# Revit family: Ladder_Caged-Access_ALACO_560-CP
name_source: partatom
category: Generic Models
units: mm (PartAtom-declared; Revit-internal decimal feet)

## family parameters
Can host rebar = No
Classification Number = 23.30.70.17.14
Cut with Voids When Loaded = No
Host = Face
Maintain Annotation Orientation = No
Part Type = Normal
Room Calculation Point = No
Round Connector Dimension = Use Diameter
Shared = No

## types (1)
- as Specified
    Assembly Code = B1010700
    Capacity = 1500 lbs per Rung
    Default Elevation = 0' - 0"
    Description = ALACO Caged Roof Hatch Access Ladder with Resting Platform - Model 560-CP as Specified
    Expected Lifespan (Years) = 0
    Keynote = 05515
    Maintenance Schedule (Months) = 0
    Manufacturer = ALACO Ladder Co
    Manufacturer Fax = 909-591-7565
    Manufacturer Website = http://alacoladder.com
    Model = 560-CP
    Product Data = http://www.arcat.com
    Revision = R1_2016-12
    Standards Conformance = OSHA ANSI A14.3
    URL = http://alacoladder.com
    Unit Width = 1' - 6"
    Warranty Duration (Years) = 0

## geometry (parser evidence)
native form markers: Sweep x12
no freeform markers — native parametric forms only
